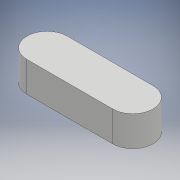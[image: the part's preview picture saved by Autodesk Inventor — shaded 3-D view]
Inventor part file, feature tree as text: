
AUTODESK INVENTOR PART (.ipt)
format: ipt  version: 2018 (Build 220112000, 112)  size: 93,184 bytes
history: native  units: mm
features: extrude x1, sketch x1
ambient origin geometry x8: Origin, YZ Plane, XZ Plane, XY Plane, X Axis, Y Axis, Z Axis, Center Point
bodies: Body1 (feature_tree)
feature tree (2):
  extrude  "Extrusión2"  Depth=8.0mm
  sketch  "Boceto1"  dims[d6=25.0mm d7=8.0mm d8=4.0mm d9=4.0mm d10=6.0mm d11=0.0mm]
